# Revit family: Nivellierbare Kassette mit Schnurauslass, RKSR, 20-25, 9
name_source: partatom
category: Generic Models
revit_build: Autodesk Revit 2015 (Build: 20140606_1530(x64)
units: mm (PartAtom-declared; Revit-internal decimal feet)

## types (4) — shared parameters
Diameter = 304 mm  [stored 0.997375 ft]
Diameter 1 = 296 mm
Height = 150 mm
Height 1 = 37 mm
HeightCalc = 150 mm
Manufacturer = OBO Bettermann
URL = http://www.obo-bettermann.com

## per-type parameters (varying)
| type | Cut depth | GTIN | Manufacturer Art.No. | Material |
| RKS2 R9 V20 | 20 mm  [stored 0.0656168 ft] | 4012195867586 | 7409278 | Stainless Steel, Polished |
| RKS2 R9 V25 | 25 mm  [stored 0.082021 ft] | 4012195867609 | 7409280 | Stainless Steel |
| RKS2 R9 M20 | 20 mm  [stored 0.0656168 ft] | 4012195867517 | 7409272 | Brass, Soft Yellow, Welded |
| RKS2 R9 M25 | 25 mm  [stored 0.082021 ft] | 4012195867579 | 7409274 | Brass, Soft Yellow, Welded |

note: column(s) folded — value = type name in every type: Article Type

note: [stored X ft] marks values corroborated as IEEE doubles in the binary element streams (Revit-internal decimal feet)

## geometry (parser evidence)
native form markers: Sweep x2
no freeform markers — native parametric forms only
